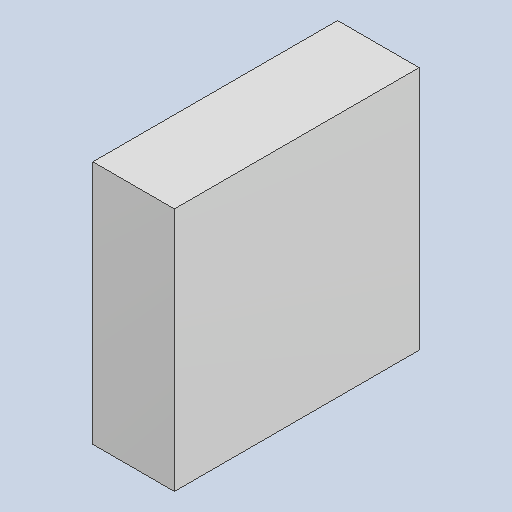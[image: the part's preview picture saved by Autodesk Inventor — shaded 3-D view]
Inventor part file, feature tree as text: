
AUTODESK INVENTOR PART (.ipt)
format: ipt  version: 2023.4 (Build 274418000, 418)  size: 81,408 bytes
history: native  units: mm
features: extrude x1
ambient origin geometry x8: Origin, YZ Plane, XZ Plane, XY Plane, X Axis, Y Axis, Z Axis, Center Point
bodies: Solid1 (feature_tree)
feature tree (1):
  extrude  "Extruded_33"  [1 undecoded]
note: 1 required parameter value undecoded (feature->parameter linkage not recoverable at this tier; creation-order binding heuristic only, values carry confidence <= 0.55)
